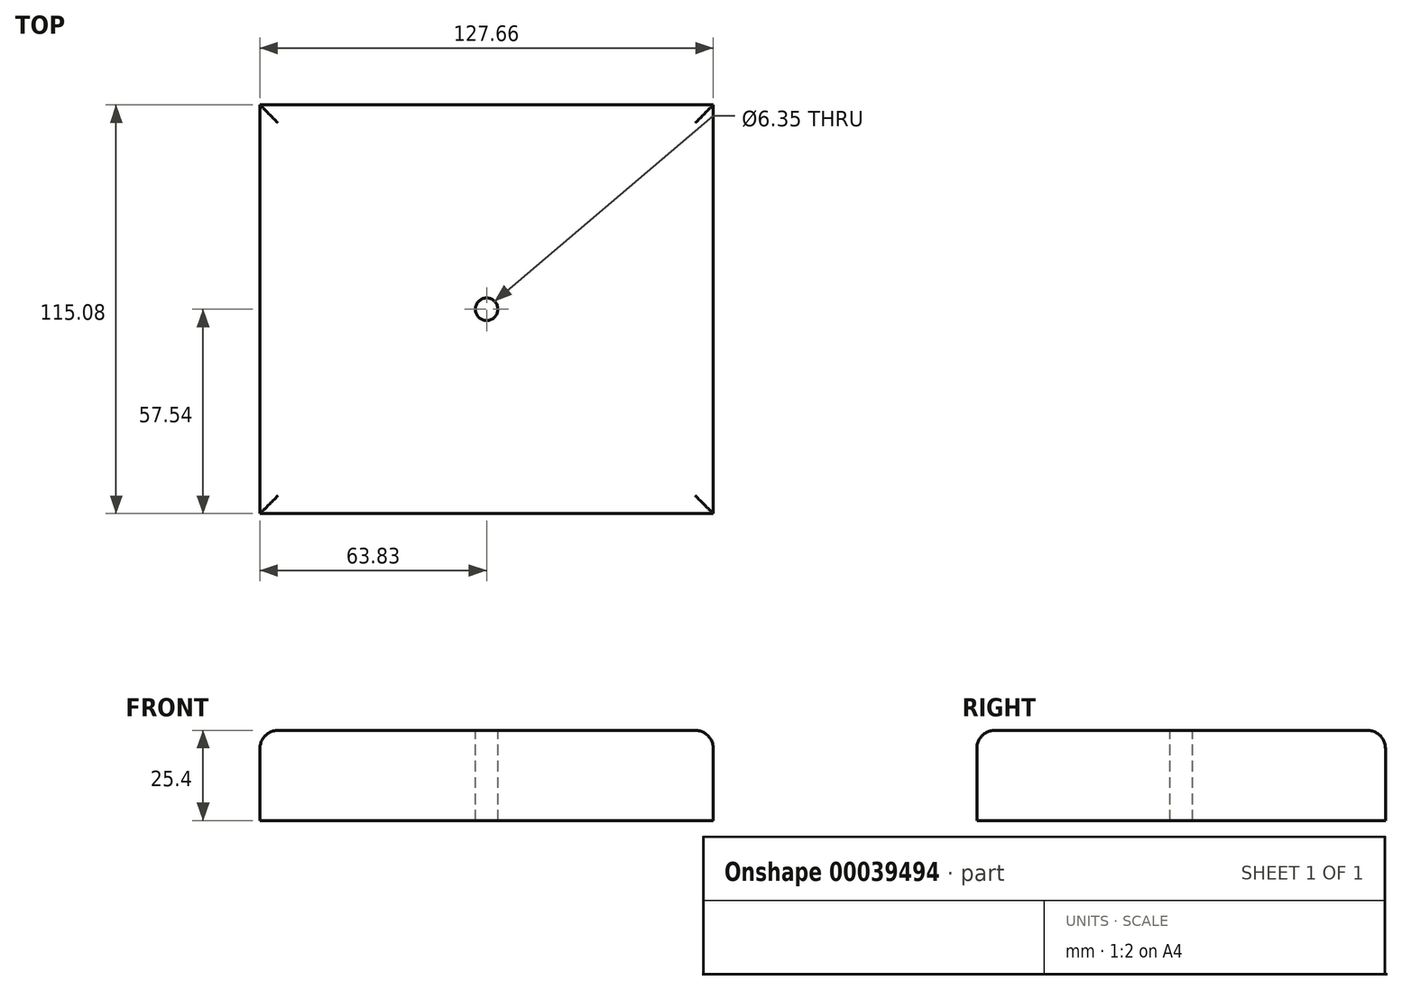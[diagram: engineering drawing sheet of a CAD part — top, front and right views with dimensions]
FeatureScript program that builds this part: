
annotation { "Feature Type Name" : "Feature", "Feature Type Description" : "" }
export const myFeature = defineFeature(function(context is Context, id is Id, definition is map)
    precondition{}
    {
        {
            var Q0;
            Q0=qCreatedBy(makeId("Top.planeOp"),FACE);
            var sketch = newSketch(context, id + "F0", { "sketchPlane" : qUnion([Q0])});
            skLineSegment(sketch, "E0.rect.bottom", {"start": v(63.83, -57.54) * mm, "end": v(-63.83, -57.54) * mm});
            skLineSegment(sketch, "E0.rect.top", {"start": v(63.83, 57.54) * mm, "end": v(-63.83, 57.54) * mm});
            skLineSegment(sketch, "E0.rect.left", {"start": v(63.83, -57.54) * mm, "end": v(63.83, 57.54) * mm});
            skLineSegment(sketch, "E0.rect.right", {"start": v(-63.83, -57.54) * mm, "end": v(-63.83, 57.54) * mm});
            skPoint(sketch, "E0.rect.middle", {"position": v(0, 0) * mm});
            skSolve(sketch);
        }
        {
            var Q0;
            Q0=makeQuery(id+"F0.imprint","IMPRINT",FACE,{"disambiguationData":[TD([[makeQuery(id+"F0.imprint","IMPRINT",EDGE,{"derivedFrom":sQuery(id+"F0.wireOp",EDGE,"E0.rect.bottom")}),-1.0]])]});
            extrude(context, id + "F1", {"entities" : qUnion([Q0]), "depth" : 25.4 * mm});
        }
        {
            var Q0;
            Q0=makeQuery(id+"F1.opExtrude","CAP_FACE",FACE,{"disambiguationData":[OSD([sQuery(id+"F0.wireOp",EDGE,"E0.rect.bottom"),sQuery(id+"F0.wireOp",EDGE,"E0.rect.top"),sQuery(id+"F0.wireOp",EDGE,"E0.rect.left"),sQuery(id+"F0.wireOp",EDGE,"E0.rect.right")])],"isStart":false});
            fillet(context, id + "F2", {"entities" : qUnion([Q0]), "radius" : 5.08 * mm, "tangentPropagation" : true, "allowEdgeOverflow" : false});
        }
        {
            var Q0;
            Q0=makeQuery(id+"F1.opExtrude","CAP_FACE",FACE,{"disambiguationData":[OSD([sQuery(id+"F0.wireOp",EDGE,"E0.rect.bottom"),sQuery(id+"F0.wireOp",EDGE,"E0.rect.top"),sQuery(id+"F0.wireOp",EDGE,"E0.rect.left"),sQuery(id+"F0.wireOp",EDGE,"E0.rect.right")])],"isStart":false});
            var sketch = newSketch(context, id + "F3", { "sketchPlane" : qUnion([Q0])});
            skPoint(sketch, "E1", {"position": v(0, 0) * mm});
            skSolve(sketch);
        }
        {
            var Q0;
            Q0=sQuery(id+"F3.wireOp",VERTEX,"E1");
            var Q1;
            Q1=makeQuery(id+"F1.opExtrude","SWEPT_BODY",BODY,{"disambiguationData":[OSD([sQuery(id+"F0.wireOp",EDGE,"E0.rect.bottom"),sQuery(id+"F0.wireOp",EDGE,"E0.rect.top"),sQuery(id+"F0.wireOp",EDGE,"E0.rect.left"),sQuery(id+"F0.wireOp",EDGE,"E0.rect.right")])]});
            hole(context, id + "F4", {"style" : HoleStyle.SIMPLE, "holeDiameter" : 6.35 * mm, "endStyle" : HoleEndStyle.THROUGH, "locations" : qUnion([Q0]), "scope" : qUnion([Q1])});
        }
    });
